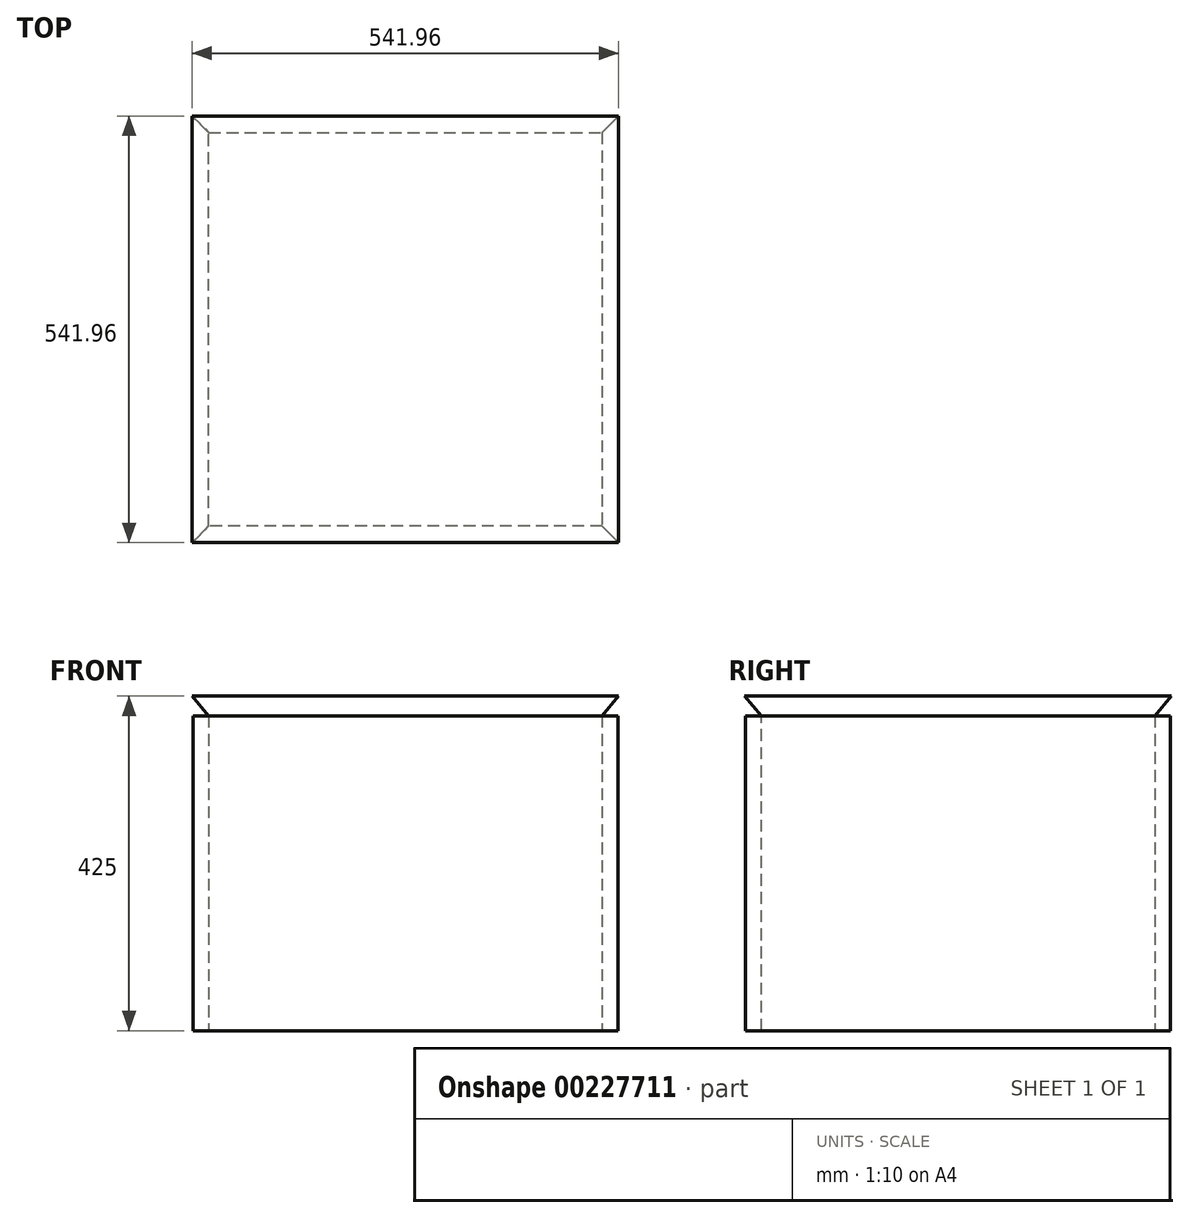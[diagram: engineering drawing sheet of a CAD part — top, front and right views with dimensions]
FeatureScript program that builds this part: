
annotation { "Feature Type Name" : "Feature", "Feature Type Description" : "" }
export const myFeature = defineFeature(function(context is Context, id is Id, definition is map)
    precondition{}
    {
        {
            var Q0;
            Q0=qCreatedBy(makeId("Top.planeOp"),FACE);
            var sketch = newSketch(context, id + "F0", { "sketchPlane" : qUnion([Q0])});
            skLineSegment(sketch, "E0.bottom", {"start": v(270, -270) * mm, "end": v(-270, -270) * mm});
            skLineSegment(sketch, "E0.top", {"start": v(270, 270) * mm, "end": v(-270, 270) * mm});
            skLineSegment(sketch, "E0.left", {"start": v(270, -270) * mm, "end": v(270, 270) * mm});
            skLineSegment(sketch, "E0.right", {"start": v(-270, -270) * mm, "end": v(-270, 270) * mm});
            skPoint(sketch, "E0.middle", {"position": v(0, 0) * mm});
            skSolve(sketch);
        }
        {
            var Q0;
            Q0 = qSketchRegion(id + "F0", true);
            var Q1;
            Q1=sQuery(id+"F0.wireOp",EDGE,"E0.bottom");
            extrude(context, id + "F1", {"entities" : qUnion([Q0]), "bodyType" : ToolBodyType.SURFACE, "surfaceEntities" : qUnion([Q1]), "depth" : 400 * mm});
        }
        {
            var Q0;
            Q0=makeQuery(id+"F1.opExtrude","SWEPT_FACE",FACE,{"disambiguationData":[OSD([sQuery(id+"F0.wireOp",EDGE,"E0.bottom")])]});
            extrude(context, id + "F2", {"entities" : qUnion([Q0]), "depth" : 20 * mm});
        }
        {
            var Q0;
            Q0=makeQuery(id+"F2.opExtrude","CAP_EDGE",EDGE,{"disambiguationData":[OSD([sQuery(id+"F0.wireOp",VERTEX,"E0.bottom.start")])],"isStart":false});
            var Q1;
            Q1=makeQuery(id+"F2.opExtrude","CAP_EDGE",EDGE,{"disambiguationData":[OSD([sQuery(id+"F0.wireOp",VERTEX,"E0.bottom.end")])],"isStart":false});
            chamfer(context, id + "F3", {"entities" : qUnion([Q0, Q1]), "width" : 20 * mm, "tangentPropagation" : true});
        }
        {
            var Q0;
            Q0=qCreatedBy(makeId("Front.planeOp"),FACE);
            var sketch = newSketch(context, id + "F4", { "sketchPlane" : qUnion([Q0])});
            skLineSegment(sketch, "E1", {"start": v(0, 0) * mm, "end": v(0, 256) * mm});
            skSolve(sketch);
        }
        {
            var Q0;
            Q0=makeQuery(id+"F2.opExtrude","SWEPT_BODY",BODY,{"disambiguationData":[OSD([sQuery(id+"F0.wireOp",EDGE,"E0.bottom")])]});
            var Q1;
            Q1=sQuery(id+"F4.wireOp",EDGE,"E1");
            circularPattern(context, id + "F5", {"entities" : qUnion([Q0]), "axis" : qUnion([Q1]), "angle" : 360 * degree, "instanceCount" : 4, "equalSpace" : true});
        }
        {
            var Q0;
            {var subQ0=sQuery(id+"F0.wireOp",EDGE,"E0.bottom");Q0=makeQuery(id+"F5.opPattern","COPY",FACE,{"derivedFrom":makeQuery(id+"F2.opExtrude","SWEPT_FACE",FACE,{"disambiguationData":[OSD([subQ0]),TDD([makeQuery(id+"F1.opExtrude","CAP_EDGE",EDGE,{"disambiguationData":[OSD([subQ0])],"isStart":false})])]}),"instanceName":"3"});}
            var sketch = newSketch(context, id + "F6", { "sketchPlane" : qUnion([Q0])});
            skLineSegment(sketch, "E2.0", {"start": v(-250, -250) * mm, "end": v(-250, 250) * mm});
            skLineSegment(sketch, "E3.0", {"start": v(250, -250) * mm, "end": v(-250, -250) * mm});
            skLineSegment(sketch, "E4.0", {"start": v(250, 250) * mm, "end": v(250, -250) * mm});
            skLineSegment(sketch, "E5.0", {"start": v(-250, 250) * mm, "end": v(250, 250) * mm});
            skSolve(sketch);
        }
        {
            var Q0;
            Q0=makeQuery(id+"F6.imprint","IMPRINT",FACE,{"disambiguationData":[TD([[makeQuery(id+"F6.imprint","IMPRINT",EDGE,{"derivedFrom":sQuery(id+"F6.wireOp",EDGE,"E2.0")}),-1.0]])]});
            extrude(context, id + "F7", {"entities" : qUnion([Q0]), "depth" : 25 * mm, "hasDraft" : true, "draftAngle" : 40 * degree});
        }
    });
